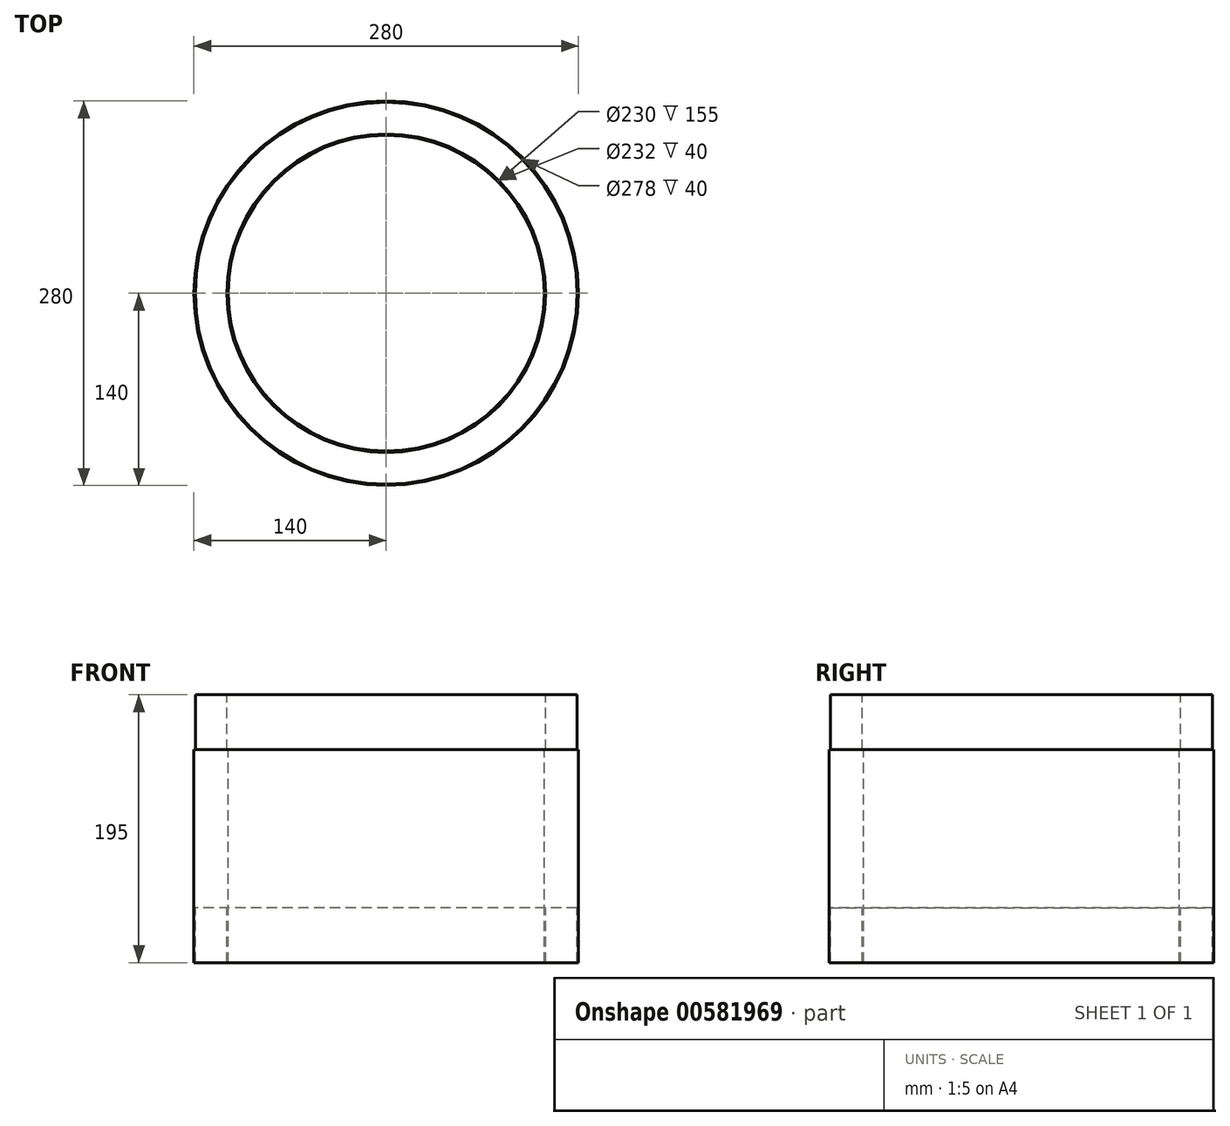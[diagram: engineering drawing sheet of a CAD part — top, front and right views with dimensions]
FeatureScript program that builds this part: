
annotation { "Feature Type Name" : "Feature", "Feature Type Description" : "" }
export const myFeature = defineFeature(function(context is Context, id is Id, definition is map)
    precondition{}
    {
        {
            var Q0;
            Q0=qCreatedBy(makeId("Front.planeOp"),FACE);
            var sketch = newSketch(context, id + "F0", { "sketchPlane" : qUnion([Q0])});
            skLineSegment(sketch, "E0", {"start": v(0, 345.75) * mm, "end": v(0, -558.03) * mm, "construction": true});
            skLineSegment(sketch, "E1", {"start": v(-115, -518.84) * mm, "end": v(-115, -363.84) * mm});
            skLineSegment(sketch, "E2", {"start": v(-115, -363.84) * mm, "end": v(-116, -363.84) * mm});
            skLineSegment(sketch, "E3", {"start": v(-116, -363.84) * mm, "end": v(-116, -323.84) * mm});
            skLineSegment(sketch, "E4", {"start": v(-116, -323.84) * mm, "end": v(-139, -323.84) * mm});
            skLineSegment(sketch, "E5", {"start": v(-139, -323.84) * mm, "end": v(-139, -363.84) * mm});
            skLineSegment(sketch, "E6", {"start": v(-139, -363.84) * mm, "end": v(-140, -363.84) * mm});
            skLineSegment(sketch, "E7", {"start": v(-140, -363.84) * mm, "end": v(-140, -518.84) * mm});
            skLineSegment(sketch, "E8", {"start": v(-140, -518.84) * mm, "end": v(-139, -518.84) * mm});
            skLineSegment(sketch, "E9", {"start": v(-139, -518.84) * mm, "end": v(-139, -478.84) * mm});
            skLineSegment(sketch, "E10", {"start": v(-139, -478.84) * mm, "end": v(-116, -478.84) * mm});
            skLineSegment(sketch, "E11", {"start": v(-116, -478.84) * mm, "end": v(-116, -518.84) * mm});
            skLineSegment(sketch, "E12", {"start": v(-116, -518.84) * mm, "end": v(-115, -518.84) * mm});
            skSolve(sketch);
        }
        {
            var Q0;
            Q0=qSketchRegion(id+"F0",true);
            var Q1;
            Q1=sQuery(id+"F0.wireOp",EDGE,"E0");
            revolve(context, id + "F1", {"entities" : qUnion([Q0]), "axis" : qUnion([Q1]), "revolveType" : RevolveType.FULL});
        }
    });
